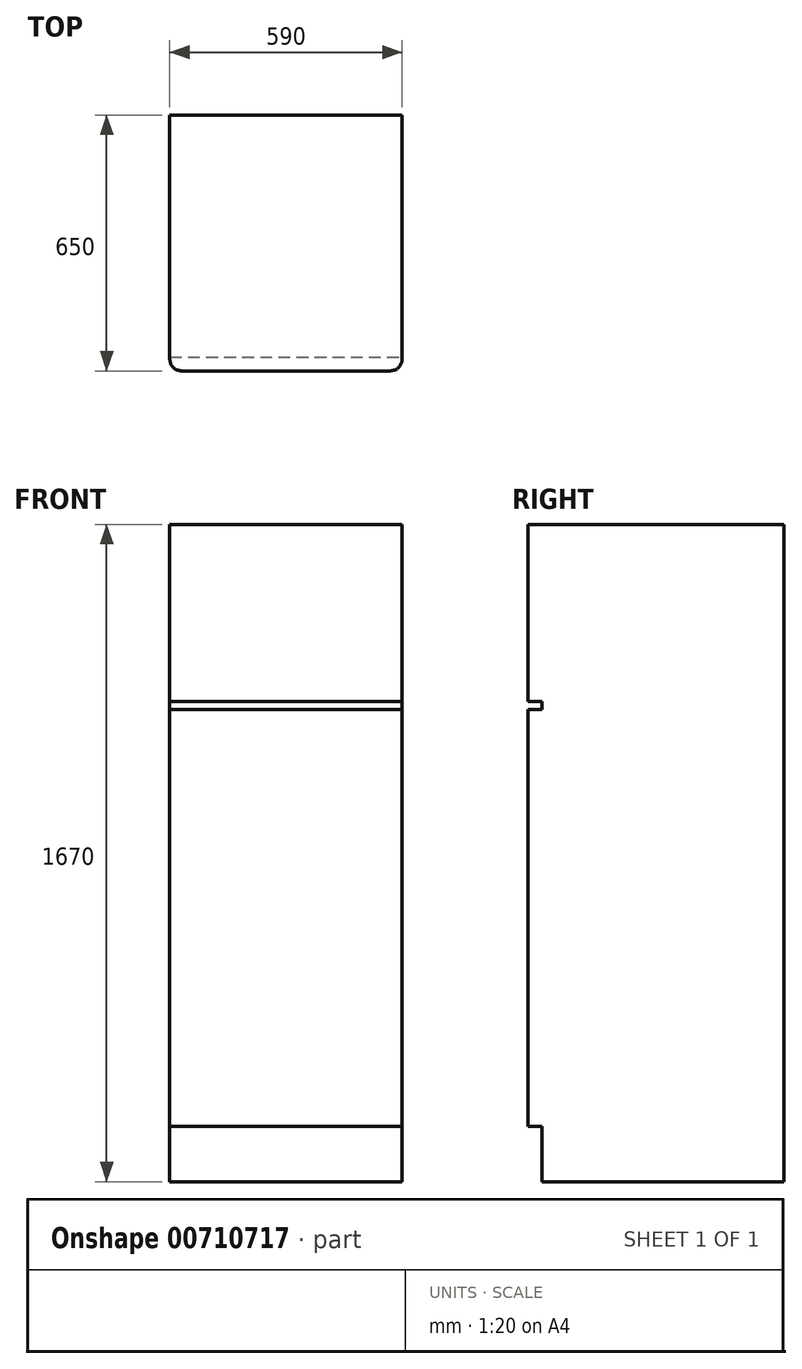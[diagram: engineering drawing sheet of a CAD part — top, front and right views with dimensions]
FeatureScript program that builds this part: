
annotation { "Feature Type Name" : "Feature", "Feature Type Description" : "" }
export const myFeature = defineFeature(function(context is Context, id is Id, definition is map)
    precondition{}
    {
        {
            assignVariable(context, id + "F0", {"name" : "hauteur", "anyValue" : 1670});
        }
        {
            var Q0;
            Q0=qCreatedBy(makeId("Top.planeOp"),FACE);
            var sketch = newSketch(context, id + "F1", { "sketchPlane" : qUnion([Q0])});
            skLineSegment(sketch, "E0.bottom", {"start": v(0, 0) * mm, "end": v(590, 0) * mm});
            skLineSegment(sketch, "E0.top", {"start": v(0, 650) * mm, "end": v(590, 650) * mm});
            skLineSegment(sketch, "E0.left", {"start": v(0, 0) * mm, "end": v(0, 650) * mm});
            skLineSegment(sketch, "E0.right", {"start": v(590, 0) * mm, "end": v(590, 650) * mm});
            skSolve(sketch);
        }
        {
            var Q0;
            Q0=qSketchRegion(id+"F1",true);
            extrude(context, id + "F2", {"entities" : qUnion([Q0]), "depth" : (getVariable(context, 'hauteur')) * mm, "offsetDistance" : 25 * mm});
        }
        {
            var Q0;
            Q0=makeQuery(id+"F2.opExtrude","SWEPT_FACE",FACE,{"disambiguationData":[OSD([sQuery(id+"F1.wireOp",EDGE,"E0.right")])]});
            var sketch = newSketch(context, id + "F3", { "sketchPlane" : qUnion([Q0])});
            skLineSegment(sketch, "E1.bottom", {"start": v(0, 0) * mm, "end": v(35, 0) * mm});
            skLineSegment(sketch, "E1.top", {"start": v(0, 140) * mm, "end": v(35, 140) * mm});
            skLineSegment(sketch, "E1.left", {"start": v(0, 0) * mm, "end": v(0, 140) * mm});
            skLineSegment(sketch, "E1.right", {"start": v(35, 0) * mm, "end": v(35, 140) * mm});
            skLineSegment(sketch, "E2.bottom", {"start": v(0, 1220) * mm, "end": v(35, 1220) * mm});
            skLineSegment(sketch, "E2.top", {"start": v(0, 1200) * mm, "end": v(35, 1200) * mm});
            skLineSegment(sketch, "E2.left", {"start": v(0, 1220) * mm, "end": v(0, 1200) * mm});
            skLineSegment(sketch, "E2.right", {"start": v(35, 1220) * mm, "end": v(35, 1200) * mm});
            skSolve(sketch);
        }
        {
            var Q0;
            Q0=qSketchRegion(id+"F3",true);
            extrude(context, id + "F4", {"entities" : qUnion([Q0]), "operationType" : NewBodyOperationType.REMOVE, "endBound" : BoundingType.THROUGH_ALL, "oppositeDirection" : true, "depth" : 25 * mm, "offsetDistance" : 25 * mm});
        }
        {
            var Q0;
            {var subQ0=sQuery(id+"F1.wireOp",EDGE,"E0.bottom");var subQ1=sQuery(id+"F1.wireOp",EDGE,"E0.left");Q0=makeQuery(id+"F4.boolean.opBoolean","SPLIT",EDGE,{"disambiguationData":[TD([makeQuery(id+"F4.opExtrude","SWEPT_FACE",FACE,{"disambiguationData":[OSD([sQuery(id+"F3.wireOp",EDGE,"E2.bottom")])]})])],"derivedFrom":makeQuery(id+"F2.opExtrude","SWEPT_EDGE",EDGE,{"disambiguationData":[OSD([subQ0,subQ1])]})});}
            var Q1;
            {var subQ0=sQuery(id+"F1.wireOp",EDGE,"E0.bottom");var subQ1=sQuery(id+"F1.wireOp",EDGE,"E0.left");Q1=makeQuery(id+"F4.boolean.opBoolean","SPLIT",EDGE,{"disambiguationData":[TD([makeQuery(id+"F4.opExtrude","SWEPT_FACE",FACE,{"disambiguationData":[OSD([sQuery(id+"F3.wireOp",EDGE,"E1.top")])]})])],"derivedFrom":makeQuery(id+"F2.opExtrude","SWEPT_EDGE",EDGE,{"disambiguationData":[OSD([subQ0,subQ1])]})});}
            var Q2;
            {var subQ0=sQuery(id+"F1.wireOp",EDGE,"E0.bottom");var subQ1=sQuery(id+"F1.wireOp",EDGE,"E0.right");Q2=makeQuery(id+"F4.boolean.opBoolean","SPLIT",EDGE,{"disambiguationData":[TD([makeQuery(id+"F4.opExtrude","SWEPT_FACE",FACE,{"disambiguationData":[OSD([sQuery(id+"F3.wireOp",EDGE,"E1.top")])]})])],"derivedFrom":makeQuery(id+"F2.opExtrude","SWEPT_EDGE",EDGE,{"disambiguationData":[OSD([subQ0,subQ1])]})});}
            var Q3;
            {var subQ0=sQuery(id+"F1.wireOp",EDGE,"E0.bottom");var subQ1=sQuery(id+"F1.wireOp",EDGE,"E0.right");Q3=makeQuery(id+"F4.boolean.opBoolean","SPLIT",EDGE,{"disambiguationData":[TD([makeQuery(id+"F4.opExtrude","SWEPT_FACE",FACE,{"disambiguationData":[OSD([sQuery(id+"F3.wireOp",EDGE,"E2.bottom")])]})])],"derivedFrom":makeQuery(id+"F2.opExtrude","SWEPT_EDGE",EDGE,{"disambiguationData":[OSD([subQ0,subQ1])]})});}
            fillet(context, id + "F5", {"entities" : qUnion([Q0, Q1, Q2, Q3]), "radius" : 30 * mm, "tangentPropagation" : true, "allowEdgeOverflow" : false});
        }
    });
